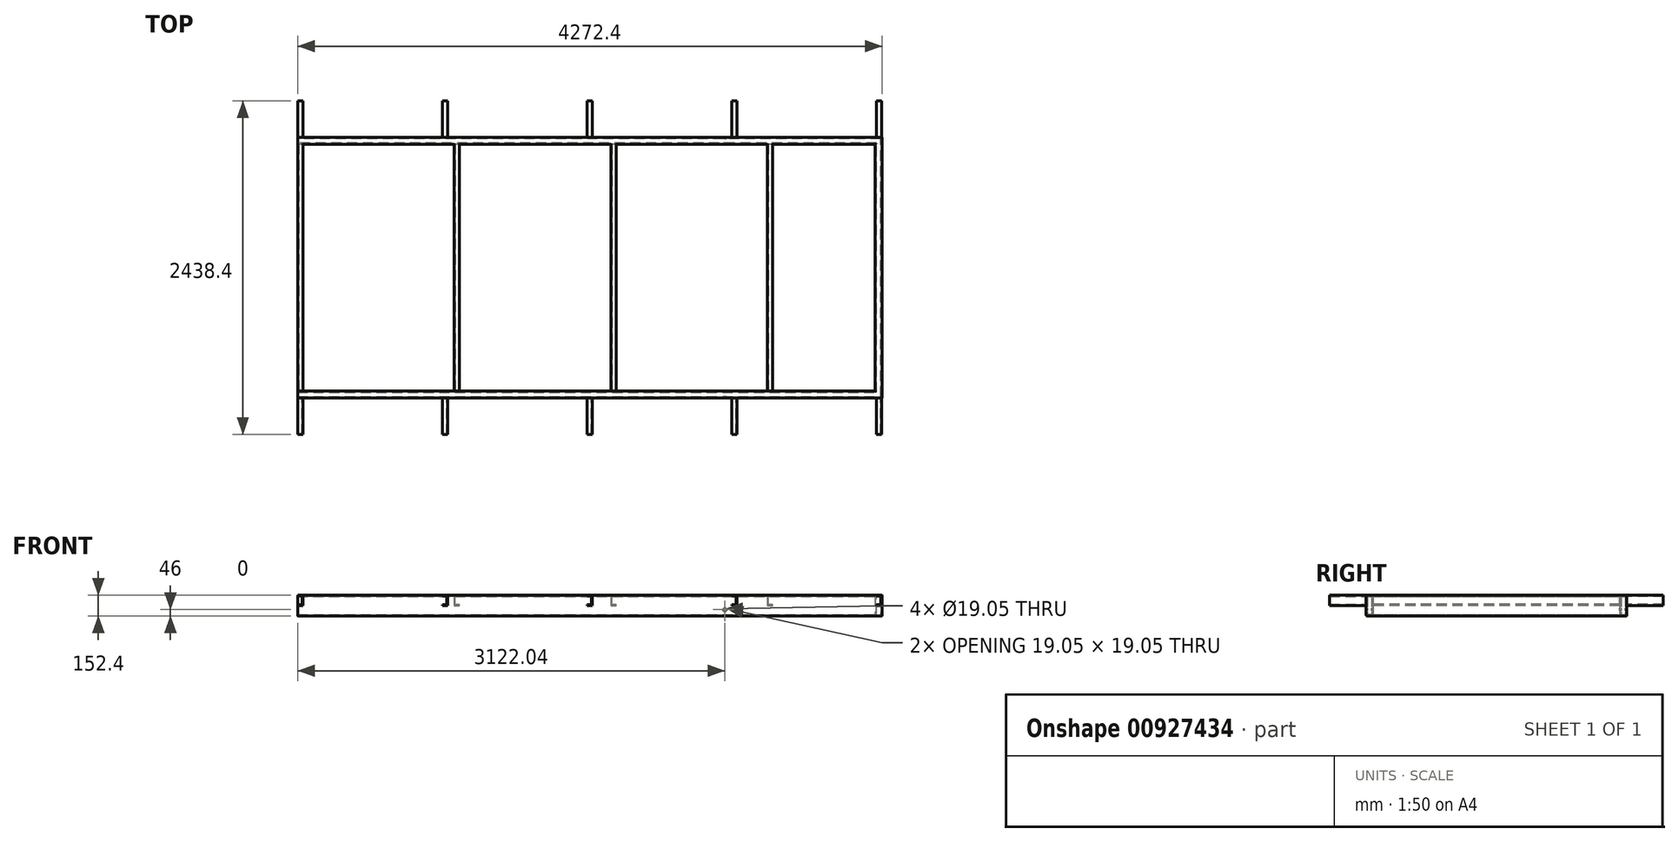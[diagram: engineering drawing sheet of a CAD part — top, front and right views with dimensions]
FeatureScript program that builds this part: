
annotation { "Feature Type Name" : "Feature", "Feature Type Description" : "" }
export const myFeature = defineFeature(function(context is Context, id is Id, definition is map)
    precondition{}
    {
        {
            var Q0;
            Q0=qCreatedBy(makeId("Top.planeOp"),FACE);
            var sketch = newSketch(context, id + "F0", { "sketchPlane" : qUnion([Q0])});
            skLineSegment(sketch, "E0.bottom", {"start": v(0, 0) * mm, "end": v(4221.6, 0) * mm});
            skLineSegment(sketch, "E0.top", {"start": v(0, 1803.4) * mm, "end": v(4221.6, 1803.4) * mm});
            skLineSegment(sketch, "E0.right", {"start": v(4221.6, 0) * mm, "end": v(4221.6, 1803.4) * mm});
            skSolve(sketch);
        }
        {
            var Q0;
            Q0=qCreatedBy(makeId("Right.planeOp"),FACE);
            var sketch = newSketch(context, id + "F1", { "sketchPlane" : qUnion([Q0])});
            skLineSegment(sketch, "E1.bottom", {"start": v(-5, 0) * mm, "end": v(-45.8, 0) * mm});
            skLineSegment(sketch, "E1.top", {"start": v(-5, -152.4) * mm, "end": v(-45.8, -152.4) * mm});
            skLineSegment(sketch, "E1.left", {"start": v(0, -5) * mm, "end": v(0, -147.4) * mm});
            skLineSegment(sketch, "E1.right", {"start": v(-50.8, -5) * mm, "end": v(-50.8, -147.4) * mm});
            skPoint(sketch, "E2.visualSharp", {"position": v(0, 0) * mm});
            skArc(sketch, "E2.filletArc", {"start": v(0, -5) * mm, "mid": v(-1.46, -1.46) * mm, "end": v(-5, 0) * mm});
            skPoint(sketch, "E3.visualSharp", {"position": v(-50.8, 0) * mm});
            skArc(sketch, "E3.filletArc", {"start": v(-45.8, 0) * mm, "mid": v(-49.34, -1.46) * mm, "end": v(-50.8, -5) * mm});
            skPoint(sketch, "E4.visualSharp", {"position": v(-50.8, -152.4) * mm});
            skArc(sketch, "E4.filletArc", {"start": v(-50.8, -147.4) * mm, "mid": v(-49.34, -150.94) * mm, "end": v(-45.8, -152.4) * mm});
            skPoint(sketch, "E5.visualSharp", {"position": v(0, -152.4) * mm});
            skArc(sketch, "E5.filletArc", {"start": v(-5, -152.4) * mm, "mid": v(-1.46, -150.94) * mm, "end": v(0, -147.4) * mm});
            skLineSegment(sketch, "E6.0", {"start": v(-9.52, -9.52) * mm, "end": v(-41.28, -9.53) * mm});
            skLineSegment(sketch, "E7.0", {"start": v(-41.28, -9.53) * mm, "end": v(-41.27, -142.88) * mm});
            skLineSegment(sketch, "E8.0", {"start": v(-9.52, -9.52) * mm, "end": v(-9.52, -142.87) * mm});
            skLineSegment(sketch, "E9.0", {"start": v(-9.52, -142.88) * mm, "end": v(-41.27, -142.88) * mm});
            skSolve(sketch);
        }
        {
            var Q0;
            Q0 = qSketchRegion(id + "F1", true);
            var Q1;
            Q1 = qConstructionFilter(qBodyType(qCreatedBy(id + "F0" ,EDGE), BodyType.WIRE), ConstructionObject.NO);
            sweep(context, id + "F2", {"profiles" : qUnion([Q0]), "path" : qUnion([Q1])});
        }
        {
            var Q0;
            Q0=makeQuery(id+"F2.opSweep","SWEPT_FACE",FACE,{"disambiguationData":[OSD([sQuery(id+"F0.wireOp",EDGE,"E0.bottom"),sQuery(id+"F1.wireOp",EDGE,"E1.left")])]});
            var sketch = newSketch(context, id + "F3", { "sketchPlane" : qUnion([Q0])});
            skLineSegment(sketch, "E10", {"start": v(-38.1, 0) * mm, "end": v(0, 0) * mm});
            skLineSegment(sketch, "E11", {"start": v(0, 0) * mm, "end": v(0, -76.2) * mm});
            skLineSegment(sketch, "E12", {"start": v(0, -76.2) * mm, "end": v(-38.1, -76.2) * mm});
            skLineSegment(sketch, "E13", {"start": v(-38.1, -76.2) * mm, "end": v(-38.1, -71.12) * mm});
            skLineSegment(sketch, "E14", {"start": v(-38.1, -71.12) * mm, "end": v(-6.35, -66.2) * mm});
            skLineSegment(sketch, "E15", {"start": v(-6.35, -66.2) * mm, "end": v(-6.35, -10) * mm});
            skLineSegment(sketch, "E16", {"start": v(-6.35, -10) * mm, "end": v(-38.1, -5.08) * mm});
            skLineSegment(sketch, "E17", {"start": v(-38.1, -5.08) * mm, "end": v(-38.1, 0) * mm});
            skLineSegment(sketch, "E18.1.0.0", {"start": v(-1150.94, -66.2) * mm, "end": v(-1150.94, -10) * mm});
            skLineSegment(sketch, "E18.1.0.1", {"start": v(-1144.59, -76.2) * mm, "end": v(-1182.69, -76.2) * mm});
            skLineSegment(sketch, "E18.1.0.2", {"start": v(-1182.69, 0) * mm, "end": v(-1144.59, 0) * mm});
            skLineSegment(sketch, "E18.1.0.3", {"start": v(-1150.94, -10) * mm, "end": v(-1182.69, -5.08) * mm});
            skLineSegment(sketch, "E18.1.0.4", {"start": v(-1182.69, -71.12) * mm, "end": v(-1150.94, -66.2) * mm});
            skLineSegment(sketch, "E18.1.0.5", {"start": v(-1144.59, 0) * mm, "end": v(-1144.59, -76.2) * mm});
            skLineSegment(sketch, "E18.1.0.6", {"start": v(-1182.69, -5.08) * mm, "end": v(-1182.69, 0) * mm});
            skLineSegment(sketch, "E18.1.0.7", {"start": v(-1182.69, -76.2) * mm, "end": v(-1182.69, -71.12) * mm});
            skLineSegment(sketch, "E18.2.0.0", {"start": v(-2295.53, -66.2) * mm, "end": v(-2295.53, -10) * mm});
            skLineSegment(sketch, "E18.2.0.1", {"start": v(-2289.18, -76.2) * mm, "end": v(-2327.28, -76.2) * mm});
            skLineSegment(sketch, "E18.2.0.2", {"start": v(-2327.28, 0) * mm, "end": v(-2289.18, 0) * mm});
            skLineSegment(sketch, "E18.2.0.3", {"start": v(-2295.53, -10) * mm, "end": v(-2327.28, -5.08) * mm});
            skLineSegment(sketch, "E18.2.0.4", {"start": v(-2327.28, -71.12) * mm, "end": v(-2295.53, -66.2) * mm});
            skLineSegment(sketch, "E18.2.0.5", {"start": v(-2289.18, 0) * mm, "end": v(-2289.18, -76.2) * mm});
            skLineSegment(sketch, "E18.2.0.6", {"start": v(-2327.28, -5.08) * mm, "end": v(-2327.28, 0) * mm});
            skLineSegment(sketch, "E18.2.0.7", {"start": v(-2327.28, -76.2) * mm, "end": v(-2327.28, -71.12) * mm});
            skLineSegment(sketch, "E18.3.0.0", {"start": v(-3440.11, -66.2) * mm, "end": v(-3440.11, -10) * mm});
            skLineSegment(sketch, "E18.3.0.1", {"start": v(-3433.76, -76.2) * mm, "end": v(-3471.86, -76.2) * mm});
            skLineSegment(sketch, "E18.3.0.2", {"start": v(-3471.86, 0) * mm, "end": v(-3433.76, 0) * mm});
            skLineSegment(sketch, "E18.3.0.3", {"start": v(-3440.11, -10) * mm, "end": v(-3471.86, -5.08) * mm});
            skLineSegment(sketch, "E18.3.0.4", {"start": v(-3471.86, -71.12) * mm, "end": v(-3440.11, -66.2) * mm});
            skLineSegment(sketch, "E18.3.0.5", {"start": v(-3433.76, 0) * mm, "end": v(-3433.76, -76.2) * mm});
            skLineSegment(sketch, "E18.3.0.6", {"start": v(-3471.86, -5.08) * mm, "end": v(-3471.86, 0) * mm});
            skLineSegment(sketch, "E18.3.0.7", {"start": v(-3471.86, -76.2) * mm, "end": v(-3471.86, -71.12) * mm});
            skLineSegment(sketch, "E18.direction1", {"start": v(-38.1, -76.2) * mm, "end": v(-1182.69, -76.2) * mm, "construction": true});
            skSolve(sketch);
        }
        {
            var Q0;
            Q0 = qSketchRegion(id + "F3", true);
            extrude(context, id + "F4", {"entities" : qUnion([Q0]), "operationType" : NewBodyOperationType.ADD, "endBound" : BoundingType.UP_TO_NEXT, "depth" : 25 * mm, "offsetDistance" : 25 * mm});
        }
        {
            var Q0;
            Q0=makeQuery(id+"F2.opSweep","SWEPT_FACE",FACE,{"disambiguationData":[OSD([sQuery(id+"F0.wireOp",EDGE,"E0.bottom"),sQuery(id+"F1.wireOp",EDGE,"E1.right")])]});
            var sketch = newSketch(context, id + "F5", { "sketchPlane" : qUnion([Q0])});
            skLineSegment(sketch, "E19", {"start": v(0, 0) * mm, "end": v(38.1, 0) * mm});
            skLineSegment(sketch, "E20", {"start": v(38.1, 0) * mm, "end": v(38.1, -76.2) * mm});
            skLineSegment(sketch, "E21", {"start": v(38.1, -76.2) * mm, "end": v(0, -76.2) * mm});
            skLineSegment(sketch, "E22", {"start": v(0, -76.2) * mm, "end": v(0, -71.12) * mm});
            skLineSegment(sketch, "E23", {"start": v(0, -71.12) * mm, "end": v(31.75, -66.2) * mm});
            skLineSegment(sketch, "E24", {"start": v(31.75, -66.2) * mm, "end": v(31.75, -10) * mm});
            skLineSegment(sketch, "E25", {"start": v(31.75, -10) * mm, "end": v(0, -5.08) * mm});
            skLineSegment(sketch, "E26", {"start": v(0, -5.08) * mm, "end": v(0, 0) * mm});
            skLineSegment(sketch, "E27.1.0.0", {"start": v(1089.66, -10) * mm, "end": v(1057.9, -5.08) * mm});
            skLineSegment(sketch, "E27.1.0.1", {"start": v(1057.9, -71.12) * mm, "end": v(1089.66, -66.2) * mm});
            skLineSegment(sketch, "E27.1.0.2", {"start": v(1096.01, 0) * mm, "end": v(1096.01, -76.2) * mm});
            skLineSegment(sketch, "E27.1.0.3", {"start": v(1057.9, 0) * mm, "end": v(1096.01, 0) * mm});
            skLineSegment(sketch, "E27.1.0.4", {"start": v(1096.01, -76.2) * mm, "end": v(1057.9, -76.2) * mm});
            skLineSegment(sketch, "E27.1.0.5", {"start": v(1089.66, -66.2) * mm, "end": v(1089.66, -10) * mm});
            skLineSegment(sketch, "E27.1.0.6", {"start": v(1057.9, -5.08) * mm, "end": v(1057.9, 0) * mm});
            skLineSegment(sketch, "E27.1.0.7", {"start": v(1057.9, -76.2) * mm, "end": v(1057.9, -71.12) * mm});
            skLineSegment(sketch, "E27.2.0.0", {"start": v(2147.57, -10) * mm, "end": v(2115.82, -5.08) * mm});
            skLineSegment(sketch, "E27.2.0.1", {"start": v(2115.82, -71.12) * mm, "end": v(2147.57, -66.2) * mm});
            skLineSegment(sketch, "E27.2.0.2", {"start": v(2153.92, 0) * mm, "end": v(2153.92, -76.2) * mm});
            skLineSegment(sketch, "E27.2.0.3", {"start": v(2115.82, 0) * mm, "end": v(2153.92, 0) * mm});
            skLineSegment(sketch, "E27.2.0.4", {"start": v(2153.92, -76.2) * mm, "end": v(2115.82, -76.2) * mm});
            skLineSegment(sketch, "E27.2.0.5", {"start": v(2147.57, -66.2) * mm, "end": v(2147.57, -10) * mm});
            skLineSegment(sketch, "E27.2.0.6", {"start": v(2115.82, -5.08) * mm, "end": v(2115.82, 0) * mm});
            skLineSegment(sketch, "E27.2.0.7", {"start": v(2115.82, -76.2) * mm, "end": v(2115.82, -71.12) * mm});
            skLineSegment(sketch, "E27.3.0.0", {"start": v(3205.48, -10) * mm, "end": v(3173.73, -5.08) * mm});
            skLineSegment(sketch, "E27.3.0.1", {"start": v(3173.73, -71.12) * mm, "end": v(3205.48, -66.2) * mm});
            skLineSegment(sketch, "E27.3.0.2", {"start": v(3211.83, 0) * mm, "end": v(3211.83, -76.2) * mm});
            skLineSegment(sketch, "E27.3.0.3", {"start": v(3173.73, 0) * mm, "end": v(3211.83, 0) * mm});
            skLineSegment(sketch, "E27.3.0.4", {"start": v(3211.83, -76.2) * mm, "end": v(3173.73, -76.2) * mm});
            skLineSegment(sketch, "E27.3.0.5", {"start": v(3205.48, -66.2) * mm, "end": v(3205.48, -10) * mm});
            skLineSegment(sketch, "E27.3.0.6", {"start": v(3173.73, -5.08) * mm, "end": v(3173.73, 0) * mm});
            skLineSegment(sketch, "E27.3.0.7", {"start": v(3173.73, -76.2) * mm, "end": v(3173.73, -71.12) * mm});
            skLineSegment(sketch, "E27.4.0.0", {"start": v(4263.4, -10) * mm, "end": v(4231.64, -5.08) * mm});
            skLineSegment(sketch, "E27.4.0.1", {"start": v(4231.64, -71.12) * mm, "end": v(4263.4, -66.2) * mm});
            skLineSegment(sketch, "E27.4.0.2", {"start": v(4269.74, 0) * mm, "end": v(4269.74, -76.2) * mm});
            skLineSegment(sketch, "E27.4.0.3", {"start": v(4231.64, 0) * mm, "end": v(4269.74, 0) * mm});
            skLineSegment(sketch, "E27.4.0.4", {"start": v(4269.74, -76.2) * mm, "end": v(4231.64, -76.2) * mm});
            skLineSegment(sketch, "E27.4.0.5", {"start": v(4263.4, -66.2) * mm, "end": v(4263.4, -10) * mm});
            skLineSegment(sketch, "E27.4.0.6", {"start": v(4231.64, -5.08) * mm, "end": v(4231.64, 0) * mm});
            skLineSegment(sketch, "E27.4.0.7", {"start": v(4231.64, -76.2) * mm, "end": v(4231.64, -71.12) * mm});
            skLineSegment(sketch, "E27.direction1", {"start": v(0, -76.2) * mm, "end": v(1057.9, -76.2) * mm, "construction": true});
            skSolve(sketch);
        }
        {
            var Q0;
            {var subQ0=sQuery(id+"F5.wireOp",EDGE,"E21");Q0=makeQuery(id+"F5.imprint","IMPRINT",FACE,{"disambiguationData":[TD([[makeQuery(id+"F5.imprint","IMPRINT",EDGE,{"derivedFrom":subQ0}),-1.0]])]});}
            var Q1;
            {var subQ4=sQuery(id+"F5.wireOp",EDGE,"E27.1.0.0");Q1=makeQuery(id+"F5.imprint","IMPRINT",FACE,{"disambiguationData":[TD([[makeQuery(id+"F5.imprint","IMPRINT",EDGE,{"derivedFrom":subQ4}),-1.0]])]});}
            var Q2;
            {var subQ4=sQuery(id+"F5.wireOp",EDGE,"E27.2.0.0");Q2=makeQuery(id+"F5.imprint","IMPRINT",FACE,{"disambiguationData":[TD([[makeQuery(id+"F5.imprint","IMPRINT",EDGE,{"derivedFrom":subQ4}),-1.0]])]});}
            var Q3;
            {var subQ4=sQuery(id+"F5.wireOp",EDGE,"E27.3.0.0");Q3=makeQuery(id+"F5.imprint","IMPRINT",FACE,{"disambiguationData":[TD([[makeQuery(id+"F5.imprint","IMPRINT",EDGE,{"derivedFrom":subQ4}),-1.0]])]});}
            var Q4;
            {var subQ6=sQuery(id+"F5.wireOp",EDGE,"E27.4.0.0");Q4=makeQuery(id+"F5.imprint","IMPRINT",FACE,{"disambiguationData":[TD([[makeQuery(id+"F5.imprint","IMPRINT",EDGE,{"derivedFrom":subQ6}),-1.0]])]});}
            var Q5;
            {var subQ0=sQuery(id+"F5.wireOp",EDGE,"E27.4.0.3");Q5=makeQuery(id+"F5.imprint","IMPRINT",FACE,{"disambiguationData":[TD([[makeQuery(id+"F5.imprint","IMPRINT",EDGE,{"derivedFrom":subQ0}),-1.0]])]});}
            var Q6;
            {var subQ0=sQuery(id+"F5.wireOp",EDGE,"E27.3.0.3");Q6=makeQuery(id+"F5.imprint","IMPRINT",FACE,{"disambiguationData":[TD([[makeQuery(id+"F5.imprint","IMPRINT",EDGE,{"derivedFrom":subQ0}),-1.0]])]});}
            var Q7;
            {var subQ0=sQuery(id+"F5.wireOp",EDGE,"E27.2.0.3");Q7=makeQuery(id+"F5.imprint","IMPRINT",FACE,{"disambiguationData":[TD([[makeQuery(id+"F5.imprint","IMPRINT",EDGE,{"derivedFrom":subQ0}),-1.0]])]});}
            var Q8;
            {var subQ0=sQuery(id+"F5.wireOp",EDGE,"E27.1.0.3");Q8=makeQuery(id+"F5.imprint","IMPRINT",FACE,{"disambiguationData":[TD([[makeQuery(id+"F5.imprint","IMPRINT",EDGE,{"derivedFrom":subQ0}),-1.0]])]});}
            var Q9;
            {var subQ0=sQuery(id+"F5.wireOp",EDGE,"E19");Q9=makeQuery(id+"F5.imprint","IMPRINT",FACE,{"disambiguationData":[TD([[makeQuery(id+"F5.imprint","IMPRINT",EDGE,{"derivedFrom":subQ0}),-1.0]])]});}
            extrude(context, id + "F6", {"entities" : qUnion([Q0, Q1, Q2, Q3, Q4, Q5, Q6, Q7, Q8, Q9]), "operationType" : NewBodyOperationType.ADD, "depth" : 266.7 * mm, "offsetDistance" : 25 * mm});
        }
        {
            var Q0;
            Q0=makeQuery(id+"F2.opSweep","SWEPT_FACE",FACE,{"disambiguationData":[OSD([sQuery(id+"F0.wireOp",EDGE,"E0.top"),sQuery(id+"F1.wireOp",EDGE,"E1.right")])]});
            var sketch = newSketch(context, id + "F7", { "sketchPlane" : qUnion([Q0])});
            skLineSegment(sketch, "E28", {"start": v(-38.1, 0) * mm, "end": v(-38.1, -76.2) * mm});
            skLineSegment(sketch, "E29.MirrorCS", {"start": v(0, -76.2) * mm, "end": v(0, -71.12) * mm});
            skLineSegment(sketch, "E30.MirrorCS", {"start": v(0, -5.08) * mm, "end": v(0, 0) * mm});
            skLineSegment(sketch, "E31.MirrorCS", {"start": v(-31.75, -66.2) * mm, "end": v(-31.75, -10) * mm});
            skLineSegment(sketch, "E32.MirrorCS", {"start": v(0, -71.12) * mm, "end": v(-31.75, -66.2) * mm});
            skLineSegment(sketch, "E33.MirrorCS", {"start": v(-38.1, -76.2) * mm, "end": v(0, -76.2) * mm});
            skLineSegment(sketch, "E34.MirrorCS", {"start": v(-31.75, -10) * mm, "end": v(0, -5.08) * mm});
            skLineSegment(sketch, "E35.MirrorCS", {"start": v(0, 0) * mm, "end": v(-38.1, 0) * mm});
            skLineSegment(sketch, "E36.1.0.0", {"start": v(-1089.66, -10) * mm, "end": v(-1057.9, -5.08) * mm});
            skLineSegment(sketch, "E36.1.0.1", {"start": v(-1096.01, 0) * mm, "end": v(-1096.01, -76.2) * mm});
            skLineSegment(sketch, "E36.1.0.2", {"start": v(-1057.9, 0) * mm, "end": v(-1096.01, 0) * mm});
            skLineSegment(sketch, "E36.1.0.3", {"start": v(-1096.01, -76.2) * mm, "end": v(-1057.9, -76.2) * mm});
            skLineSegment(sketch, "E36.1.0.4", {"start": v(-1089.66, -66.2) * mm, "end": v(-1089.66, -10) * mm});
            skLineSegment(sketch, "E36.1.0.5", {"start": v(-1057.9, -71.12) * mm, "end": v(-1089.66, -66.2) * mm});
            skLineSegment(sketch, "E36.1.0.6", {"start": v(-1057.9, -76.2) * mm, "end": v(-1057.9, -71.12) * mm});
            skLineSegment(sketch, "E36.1.0.7", {"start": v(-1057.9, -5.08) * mm, "end": v(-1057.9, 0) * mm});
            skLineSegment(sketch, "E36.2.0.0", {"start": v(-2147.57, -10) * mm, "end": v(-2115.82, -5.08) * mm});
            skLineSegment(sketch, "E36.2.0.1", {"start": v(-2153.92, 0) * mm, "end": v(-2153.92, -76.2) * mm});
            skLineSegment(sketch, "E36.2.0.2", {"start": v(-2115.82, 0) * mm, "end": v(-2153.92, 0) * mm});
            skLineSegment(sketch, "E36.2.0.3", {"start": v(-2153.92, -76.2) * mm, "end": v(-2115.82, -76.2) * mm});
            skLineSegment(sketch, "E36.2.0.4", {"start": v(-2147.57, -66.2) * mm, "end": v(-2147.57, -10) * mm});
            skLineSegment(sketch, "E36.2.0.5", {"start": v(-2115.82, -71.12) * mm, "end": v(-2147.57, -66.2) * mm});
            skLineSegment(sketch, "E36.2.0.6", {"start": v(-2115.82, -76.2) * mm, "end": v(-2115.82, -71.12) * mm});
            skLineSegment(sketch, "E36.2.0.7", {"start": v(-2115.82, -5.08) * mm, "end": v(-2115.82, 0) * mm});
            skLineSegment(sketch, "E36.3.0.0", {"start": v(-3205.48, -10) * mm, "end": v(-3173.73, -5.08) * mm});
            skLineSegment(sketch, "E36.3.0.1", {"start": v(-3211.83, 0) * mm, "end": v(-3211.83, -76.2) * mm});
            skLineSegment(sketch, "E36.3.0.2", {"start": v(-3173.73, 0) * mm, "end": v(-3211.83, 0) * mm});
            skLineSegment(sketch, "E36.3.0.3", {"start": v(-3211.83, -76.2) * mm, "end": v(-3173.73, -76.2) * mm});
            skLineSegment(sketch, "E36.3.0.4", {"start": v(-3205.48, -66.2) * mm, "end": v(-3205.48, -10) * mm});
            skLineSegment(sketch, "E36.3.0.5", {"start": v(-3173.73, -71.12) * mm, "end": v(-3205.48, -66.2) * mm});
            skLineSegment(sketch, "E36.3.0.6", {"start": v(-3173.73, -76.2) * mm, "end": v(-3173.73, -71.12) * mm});
            skLineSegment(sketch, "E36.3.0.7", {"start": v(-3173.73, -5.08) * mm, "end": v(-3173.73, 0) * mm});
            skLineSegment(sketch, "E36.4.0.0", {"start": v(-4263.4, -10) * mm, "end": v(-4231.64, -5.08) * mm});
            skLineSegment(sketch, "E36.4.0.1", {"start": v(-4269.74, 0) * mm, "end": v(-4269.74, -76.2) * mm});
            skLineSegment(sketch, "E36.4.0.2", {"start": v(-4231.64, 0) * mm, "end": v(-4269.74, 0) * mm});
            skLineSegment(sketch, "E36.4.0.3", {"start": v(-4269.74, -76.2) * mm, "end": v(-4231.64, -76.2) * mm});
            skLineSegment(sketch, "E36.4.0.4", {"start": v(-4263.4, -66.2) * mm, "end": v(-4263.4, -10) * mm});
            skLineSegment(sketch, "E36.4.0.5", {"start": v(-4231.64, -71.12) * mm, "end": v(-4263.4, -66.2) * mm});
            skLineSegment(sketch, "E36.4.0.6", {"start": v(-4231.64, -76.2) * mm, "end": v(-4231.64, -71.12) * mm});
            skLineSegment(sketch, "E36.4.0.7", {"start": v(-4231.64, -5.08) * mm, "end": v(-4231.64, 0) * mm});
            skLineSegment(sketch, "E36.direction1", {"start": v(-38.1, -76.2) * mm, "end": v(-1096.01, -76.2) * mm, "construction": true});
            skSolve(sketch);
        }
        {
            var Q0;
            Q0=makeQuery(id+"F7.imprint","IMPRINT",FACE,{"disambiguationData":[TD([[makeQuery(id+"F7.imprint","IMPRINT",EDGE,{"derivedFrom":sQuery(id+"F7.wireOp",EDGE,"E29.MirrorCS")}),-1.0]])]});
            var Q1;
            {var subQ0=sQuery(id+"F7.wireOp",EDGE,"E35.MirrorCS");Q1=makeQuery(id+"F7.imprint","IMPRINT",FACE,{"disambiguationData":[TD([[makeQuery(id+"F7.imprint","IMPRINT",EDGE,{"derivedFrom":subQ0}),1.0]])]});}
            var Q2;
            {var subQ0=sQuery(id+"F7.wireOp",EDGE,"E36.1.0.2");Q2=makeQuery(id+"F7.imprint","IMPRINT",FACE,{"disambiguationData":[TD([[makeQuery(id+"F7.imprint","IMPRINT",EDGE,{"derivedFrom":subQ0}),1.0]])]});}
            var Q3;
            {var subQ4=sQuery(id+"F7.wireOp",EDGE,"E36.1.0.0");Q3=makeQuery(id+"F7.imprint","IMPRINT",FACE,{"disambiguationData":[TD([[makeQuery(id+"F7.imprint","IMPRINT",EDGE,{"derivedFrom":subQ4}),1.0]])]});}
            var Q4;
            {var subQ4=sQuery(id+"F7.wireOp",EDGE,"E36.2.0.0");Q4=makeQuery(id+"F7.imprint","IMPRINT",FACE,{"disambiguationData":[TD([[makeQuery(id+"F7.imprint","IMPRINT",EDGE,{"derivedFrom":subQ4}),1.0]])]});}
            var Q5;
            {var subQ0=sQuery(id+"F7.wireOp",EDGE,"E36.2.0.2");Q5=makeQuery(id+"F7.imprint","IMPRINT",FACE,{"disambiguationData":[TD([[makeQuery(id+"F7.imprint","IMPRINT",EDGE,{"derivedFrom":subQ0}),1.0]])]});}
            var Q6;
            {var subQ0=sQuery(id+"F7.wireOp",EDGE,"E36.3.0.2");Q6=makeQuery(id+"F7.imprint","IMPRINT",FACE,{"disambiguationData":[TD([[makeQuery(id+"F7.imprint","IMPRINT",EDGE,{"derivedFrom":subQ0}),1.0]])]});}
            var Q7;
            {var subQ4=sQuery(id+"F7.wireOp",EDGE,"E36.3.0.0");Q7=makeQuery(id+"F7.imprint","IMPRINT",FACE,{"disambiguationData":[TD([[makeQuery(id+"F7.imprint","IMPRINT",EDGE,{"derivedFrom":subQ4}),1.0]])]});}
            var Q8;
            {var subQ0=sQuery(id+"F7.wireOp",EDGE,"E36.4.0.2");Q8=makeQuery(id+"F7.imprint","IMPRINT",FACE,{"disambiguationData":[TD([[makeQuery(id+"F7.imprint","IMPRINT",EDGE,{"derivedFrom":subQ0}),1.0]])]});}
            var Q9;
            {var subQ4=sQuery(id+"F7.wireOp",EDGE,"E36.4.0.0");Q9=makeQuery(id+"F7.imprint","IMPRINT",FACE,{"disambiguationData":[TD([[makeQuery(id+"F7.imprint","IMPRINT",EDGE,{"derivedFrom":subQ4}),1.0]])]});}
            extrude(context, id + "F8", {"entities" : qUnion([Q0, Q1, Q2, Q3, Q4, Q5, Q6, Q7, Q8, Q9]), "operationType" : NewBodyOperationType.ADD, "depth" : 266.7 * mm, "offsetDistance" : 25 * mm});
        }
        {
            var Q0;
            Q0=makeQuery(id+"F2.opSweep","SWEPT_FACE",FACE,{"disambiguationData":[OSD([sQuery(id+"F0.wireOp",EDGE,"E0.top"),sQuery(id+"F1.wireOp",EDGE,"E1.left")])]});
            var sketch = newSketch(context, id + "F9", { "sketchPlane" : qUnion([Q0])});
            skCircle(sketch, "E37", {"center": v(3122.04, -106.4) * mm, "radius": 9.53 * mm});
            skLineSegment(sketch, "E38", {"start": v(3122.04, -106.4) * mm, "end": v(3220.22, -106.4) * mm, "construction": true});
            skSolve(sketch);
        }
        {
            var Q0;
            Q0 = qSketchRegion(id + "F9", true);
            extrude(context, id + "F10", {"entities" : qUnion([Q0]), "operationType" : NewBodyOperationType.REMOVE, "endBound" : BoundingType.SYMMETRIC, "depth" : 5280 * mm, "hasOffset" : true, "offsetDistance" : 40 * mm, "offsetOppositeDirection" : true, "hasSecondDirection" : true, "secondDirectionBound" : SecondDirectionBoundingType.THROUGH_ALL, "secondDirectionOppositeDirection" : false, "secondDirectionDepth" : 1850 * mm});
        }
    });
